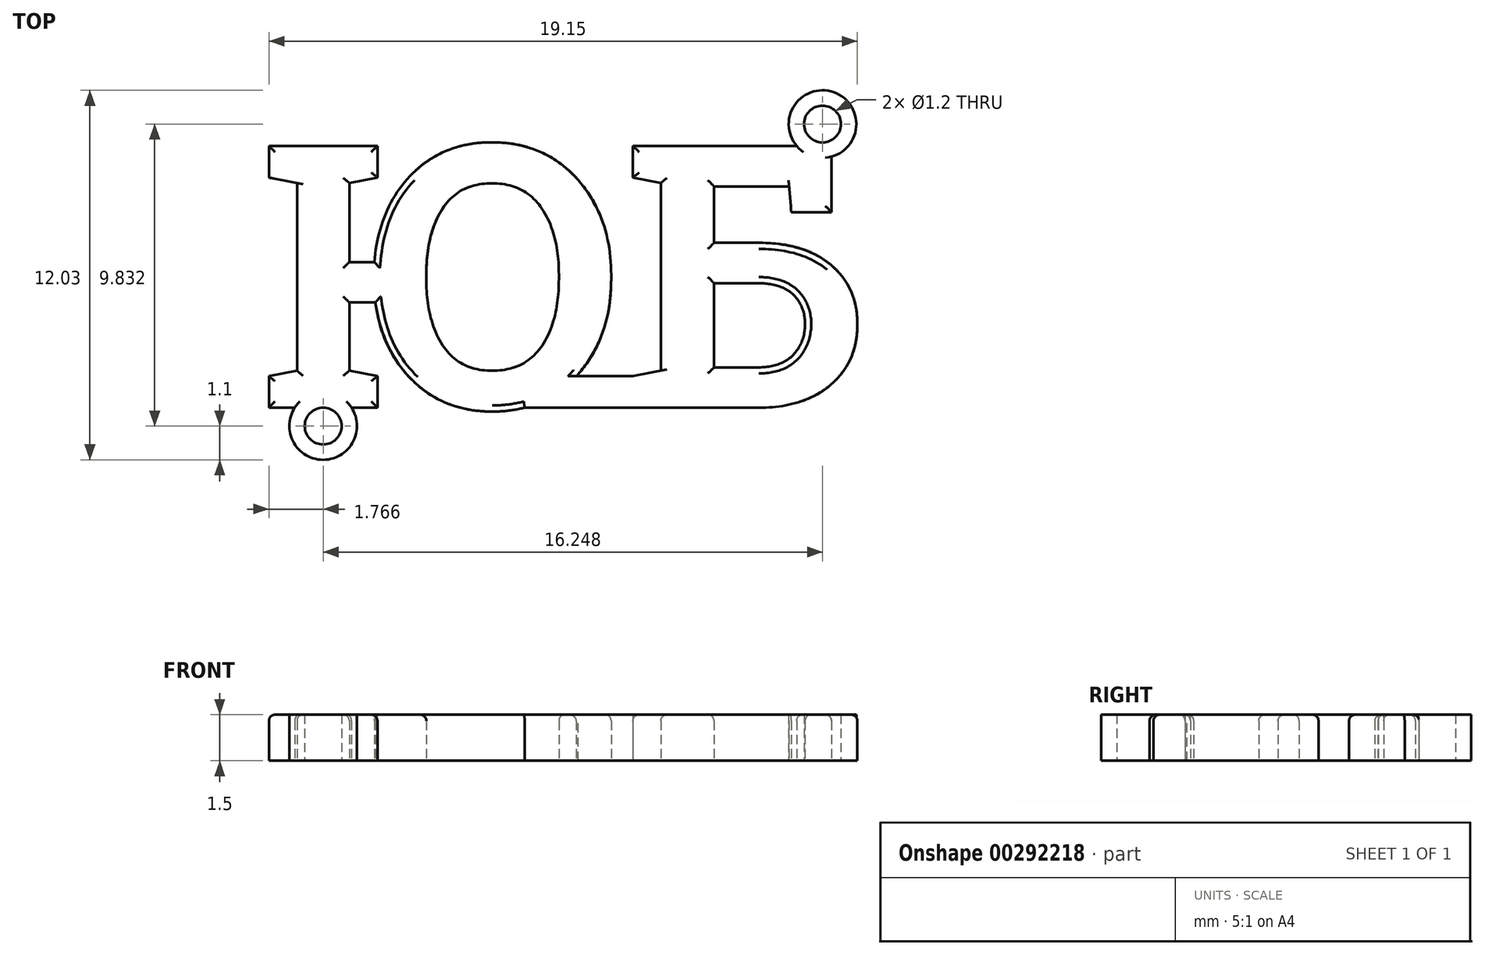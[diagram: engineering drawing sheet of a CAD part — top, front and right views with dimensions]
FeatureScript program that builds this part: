
annotation { "Feature Type Name" : "Feature", "Feature Type Description" : "" }
export const myFeature = defineFeature(function(context is Context, id is Id, definition is map)
    precondition{}
    {
        {
            var Q0;
            Q0=qCreatedBy(makeId("Top.planeOp"),FACE);
            var sketch = newSketch(context, id + "F0", { "sketchPlane" : qUnion([Q0])});
            skText(sketch, "E0", { "text": "ЮБ", "fontName": "RobotoSlab-Bold.ttf"});
            skCircle(sketch, "E1", {"center": v(-8.12, -0.6) * mm, "radius": 0.6 * mm});
            skCircle(sketch, "E2.0", {"center": v(-8.12, -0.6) * mm, "radius": 1.1 * mm});
            skPoint(sketch, "E3", {"position": v(-10, 0) * mm});
            skPoint(sketch, "E4", {"position": v(-8.12, 0) * mm});
            skPoint(sketch, "E5", {"position": v(-7.2, 0) * mm});
            skLineSegment(sketch, "E6", {"start": v(0, 0) * mm, "end": v(0, -7.24) * mm, "construction": true});
            skCircle(sketch, "E7.MirrorC", {"center": v(8.12, -0.6) * mm, "radius": 0.6 * mm, "construction": true});
            skCircle(sketch, "E8.MirrorC", {"center": v(8.12, -0.6) * mm, "radius": 1.1 * mm, "construction": true});
            skLineSegment(sketch, "E9", {"start": v(0, 4.32) * mm, "end": v(-11.86, 4.32) * mm, "construction": true});
            skPoint(sketch, "E9.endSnap0", {"position": v(-10, 4.32) * mm});
            skCircle(sketch, "E10.MirrorC", {"center": v(-8.12, 9.23) * mm, "radius": 0.6 * mm, "construction": true});
            skCircle(sketch, "E11.MirrorC", {"center": v(-8.12, 9.23) * mm, "radius": 1.1 * mm, "construction": true});
            skCircle(sketch, "E12.MirrorC", {"center": v(8.12, 9.23) * mm, "radius": 0.6 * mm});
            skLineSegment(sketch, "E13.bottom", {"start": v(1.96, 1.02) * mm, "end": v(-1.9, 1.02) * mm});
            skLineSegment(sketch, "E13.top", {"start": v(1.96, 0) * mm, "end": v(-1.9, 0) * mm});
            skLineSegment(sketch, "E13.left", {"start": v(1.96, 1.02) * mm, "end": v(1.96, 0) * mm});
            skLineSegment(sketch, "E13.right", {"start": v(-1.9, 1.02) * mm, "end": v(-1.9, 0) * mm});
            skCircle(sketch, "E14.MirrorC", {"center": v(8.12, 9.23) * mm, "radius": 1.1 * mm});
            skLineSegment(sketch, "E15", {"start": v(-9.89, 1.01) * mm, "end": v(-6.36, 1.01) * mm});
            skLineSegment(sketch, "E16", {"start": v(-8.12, 1.01) * mm, "end": v(-8.12, -0.92) * mm, "construction": true});
            const initialGuessF0  = {"E0": [-0.01, 0, 1, 0, 0.00863]};
            skSetInitialGuess(sketch, initialGuessF0);
            skSolve(sketch);
        }
        {
            var Q0;
            {var subQ9=sQuery(id+"F0.wireOp",EDGE,"cf95b76b-212f-4af7-b6d1-8cdce05abc63.top");Q0=makeQuery(id+"F0.imprint","IMPRINT",FACE,{"disambiguationData":[TD([[makeQuery(id+"F0.imprint","IMPRINT",EDGE,{"derivedFrom":subQ9}),1.0]])]});}
            var Q1;
            {var subQ1=sQuery(id+"F0.wireOp",EDGE,"E0.sketch_text.stroke-48");var subQ5=sQuery(id+"F0.wireOp",EDGE,"E0.sketch_text.stroke-47");var subQ6=makeQuery(id+"F0.imprint","INTERSECT",VERTEX,{"derivedFrom":[subQ5,subQ1]});Q1=makeQuery(id+"F0.imprint","IMPRINT",FACE,{"disambiguationData":[TD([[makeQuery(id+"F0.imprint","IMPRINT",EDGE,{"disambiguationData":[TD([[subQ6,1.0]])],"derivedFrom":subQ5}),1.0]])]});}
            var Q2;
            {var subQ1=sQuery(id+"F0.wireOp",EDGE,"E0.sketch_text.stroke-48");var subQ6=sQuery(id+"F0.wireOp",EDGE,"E0.sketch_text.stroke-47");var subQ7=makeQuery(id+"F0.imprint","INTERSECT",VERTEX,{"derivedFrom":[subQ6,subQ1]});Q2=makeQuery(id+"F0.imprint","IMPRINT",FACE,{"disambiguationData":[TD([[makeQuery(id+"F0.imprint","IMPRINT",EDGE,{"disambiguationData":[TD([[subQ7,1.0]])],"derivedFrom":subQ6}),-1.0]])]});}
            var Q3;
            {var subQ1=sQuery(id+"F0.wireOp",EDGE,"E0.sketch_text.stroke-19");var subQ6=sQuery(id+"F0.wireOp",EDGE,"E2.0");var subQ8=makeQuery(id+"F0.imprint","INTERSECT",VERTEX,{"derivedFrom":[subQ1,subQ6]});Q3=makeQuery(id+"F0.imprint","IMPRINT",FACE,{"disambiguationData":[TD([[makeQuery(id+"F0.imprint","IMPRINT",EDGE,{"disambiguationData":[TD([[subQ8,-1.0]])],"derivedFrom":subQ1}),-1.0]])]});}
            var Q4;
            {var subQ1=sQuery(id+"F0.wireOp",EDGE,"E0.sketch_text.stroke-19");var subQ3=sQuery(id+"F0.wireOp",EDGE,"E2.0");var subQ8=makeQuery(id+"F0.imprint","INTERSECT",VERTEX,{"derivedFrom":[subQ1,subQ3]});Q4=makeQuery(id+"F0.imprint","IMPRINT",FACE,{"disambiguationData":[TD([[makeQuery(id+"F0.imprint","IMPRINT",EDGE,{"disambiguationData":[TD([[subQ8,-1.0]])],"derivedFrom":subQ1}),1.0]])]});}
            var Q5;
            {var subQ1=sQuery(id+"F0.wireOp",EDGE,"E0.sketch_text.stroke-1");var subQ6=sQuery(id+"F0.wireOp",EDGE,"E0.sketch_text.stroke-0");var subQ7=makeQuery(id+"F0.imprint","INTERSECT",VERTEX,{"derivedFrom":[subQ6,subQ1]});Q5=makeQuery(id+"F0.imprint","IMPRINT",FACE,{"disambiguationData":[TD([[makeQuery(id+"F0.imprint","IMPRINT",EDGE,{"disambiguationData":[TD([[subQ7,1.0]])],"derivedFrom":subQ6}),1.0]])]});}
            var Q6;
            {var subQ0=sQuery(id+"F0.wireOp",EDGE,"E7.MirrorC");var subQ1=sQuery(id+"F0.wireOp",EDGE,"E0.sketch_text.stroke-48");var subQ2=makeQuery(id+"F0.imprint","INTERSECT",VERTEX,{"disambiguationData":[OD(0.0)],"derivedFrom":[subQ1,subQ0]});Q6=makeQuery(id+"F0.imprint","IMPRINT",FACE,{"disambiguationData":[TD([[makeQuery(id+"F0.imprint","IMPRINT",EDGE,{"disambiguationData":[TD([[subQ2,-1.0]])],"derivedFrom":subQ1}),-1.0]])]});}
            var Q7;
            {var subQ5=sQuery(id+"F0.wireOp",EDGE,"E13.right");Q7=makeQuery(id+"F0.imprint","IMPRINT",FACE,{"disambiguationData":[TD([[makeQuery(id+"F0.imprint","IMPRINT",EDGE,{"derivedFrom":subQ5}),1.0]])]});}
            var Q8;
            {var subQ0=sQuery(id+"F0.wireOp",EDGE,"E13.bottom");var subQ1=sQuery(id+"F0.wireOp",EDGE,"E0.sketch_text.stroke-12");var subQ2=makeQuery(id+"F0.imprint","INTERSECT",VERTEX,{"derivedFrom":[subQ1,subQ0]});Q8=makeQuery(id+"F0.imprint","IMPRINT",FACE,{"disambiguationData":[TD([[makeQuery(id+"F0.imprint","IMPRINT",EDGE,{"disambiguationData":[TD([[subQ2,-1.0]])],"derivedFrom":subQ1}),1.0]])]});}
            var Q9;
            {var subQ5=sQuery(id+"F0.wireOp",EDGE,"E13.left");Q9=makeQuery(id+"F0.imprint","IMPRINT",FACE,{"disambiguationData":[TD([[makeQuery(id+"F0.imprint","IMPRINT",EDGE,{"derivedFrom":subQ5}),-1.0]])]});}
            var Q10;
            {var subQ9=sQuery(id+"F0.wireOp",EDGE,"E0.sketch_text.stroke-34");Q10=makeQuery(id+"F0.imprint","IMPRINT",FACE,{"disambiguationData":[TD([[makeQuery(id+"F0.imprint","IMPRINT",EDGE,{"derivedFrom":subQ9}),-1.0]])]});}
            var Q11;
            {var subQ0=sQuery(id+"F0.wireOp",EDGE,"E14.MirrorC");var subQ1=sQuery(id+"F0.wireOp",EDGE,"E0.sketch_text.stroke-38");var subQ2=makeQuery(id+"F0.imprint","INTERSECT",VERTEX,{"derivedFrom":[subQ1,subQ0]});Q11=makeQuery(id+"F0.imprint","IMPRINT",FACE,{"disambiguationData":[TD([[makeQuery(id+"F0.imprint","IMPRINT",EDGE,{"disambiguationData":[TD([[subQ2,-1.0]])],"derivedFrom":subQ1}),1.0]])]});}
            var Q12;
            {var subQ0=sQuery(id+"F0.wireOp",EDGE,"E14.MirrorC");var subQ1=sQuery(id+"F0.wireOp",EDGE,"E0.sketch_text.stroke-38");var subQ2=makeQuery(id+"F0.imprint","INTERSECT",VERTEX,{"derivedFrom":[subQ1,subQ0]});Q12=makeQuery(id+"F0.imprint","IMPRINT",FACE,{"disambiguationData":[TD([[makeQuery(id+"F0.imprint","IMPRINT",EDGE,{"disambiguationData":[TD([[subQ2,-1.0]])],"derivedFrom":subQ1}),-1.0]])]});}
            var Q13;
            {var subQ1=sQuery(id+"F0.wireOp",EDGE,"E0.sketch_text.stroke-1");var subQ6=sQuery(id+"F0.wireOp",EDGE,"E0.sketch_text.stroke-0");var subQ7=makeQuery(id+"F0.imprint","INTERSECT",VERTEX,{"derivedFrom":[subQ6,subQ1]});Q13=makeQuery(id+"F0.imprint","IMPRINT",FACE,{"disambiguationData":[TD([[makeQuery(id+"F0.imprint","IMPRINT",EDGE,{"disambiguationData":[TD([[subQ7,1.0]])],"derivedFrom":subQ6}),-1.0]])]});}
            var Q14;
            {var subQ14=sQuery(id+"F0.wireOp",EDGE,"E0.sketch_text.stroke-2");Q14=makeQuery(id+"F0.imprint","IMPRINT",FACE,{"disambiguationData":[TD([[makeQuery(id+"F0.imprint","IMPRINT",EDGE,{"derivedFrom":subQ14}),-1.0]])]});}
            var Q15;
            {var subQ1=sQuery(id+"F0.wireOp",EDGE,"E0.sketch_text.stroke-19");var subQ6=sQuery(id+"F0.wireOp",EDGE,"E0.sketch_text.stroke-18");var subQ7=makeQuery(id+"F0.imprint","INTERSECT",VERTEX,{"derivedFrom":[subQ6,subQ1]});Q15=makeQuery(id+"F0.imprint","IMPRINT",FACE,{"disambiguationData":[TD([[makeQuery(id+"F0.imprint","IMPRINT",EDGE,{"disambiguationData":[TD([[subQ7,1.0]])],"derivedFrom":subQ6}),-1.0]])]});}
            extrude(context, id + "F1", {"entities" : qUnion([Q0, Q1, Q2, Q3, Q4, Q5, Q6, Q7, Q8, Q9, Q10, Q11, Q12, Q13, Q14, Q15]), "depth" : 1.5 * mm, "offsetDistance" : 25 * mm});
        }
        {
            var Q0;
            Q0=makeQuery(id+"F1.opExtrude","CAP_EDGE",EDGE,{"disambiguationData":[OSD([sQuery(id+"F0.wireOp",EDGE,"E0.sketch_text.stroke-39")])],"isStart":false});
            var Q1;
            Q1=makeQuery(id+"F1.opExtrude","CAP_EDGE",EDGE,{"disambiguationData":[OSD([sQuery(id+"F0.wireOp",EDGE,"E0.sketch_text.stroke-6")])],"isStart":false});
            var Q2;
            Q2=makeQuery(id+"F1.opExtrude","CAP_EDGE",EDGE,{"disambiguationData":[OSD([sQuery(id+"F0.wireOp",EDGE,"E0.sketch_text.stroke-1")])],"isStart":false});
            var Q3;
            Q3=makeQuery(id+"F1.opExtrude","CAP_EDGE",EDGE,{"disambiguationData":[OSD([sQuery(id+"F0.wireOp",EDGE,"E0.sketch_text.stroke-22")])],"isStart":false});
            var Q4;
            Q4=makeQuery(id+"F1.opExtrude","CAP_EDGE",EDGE,{"disambiguationData":[OSD([sQuery(id+"F0.wireOp",EDGE,"E0.sketch_text.stroke-0")])],"isStart":false});
            var Q5;
            Q5=makeQuery(id+"F1.opExtrude","CAP_EDGE",EDGE,{"disambiguationData":[OSD([sQuery(id+"F0.wireOp",EDGE,"E0.sketch_text.stroke-3")])],"isStart":false});
            var Q6;
            Q6=makeQuery(id+"F1.opExtrude","CAP_EDGE",EDGE,{"disambiguationData":[OSD([sQuery(id+"F0.wireOp",EDGE,"E0.sketch_text.stroke-2")])],"isStart":false});
            var Q7;
            Q7=makeQuery(id+"F1.opExtrude","CAP_EDGE",EDGE,{"disambiguationData":[OSD([sQuery(id+"F0.wireOp",EDGE,"E0.sketch_text.stroke-4")])],"isStart":false});
            var Q8;
            Q8=makeQuery(id+"F1.opExtrude","CAP_EDGE",EDGE,{"disambiguationData":[OSD([sQuery(id+"F0.wireOp",EDGE,"E0.sketch_text.stroke-5")])],"isStart":false});
            var Q9;
            Q9=makeQuery(id+"F1.opExtrude","CAP_EDGE",EDGE,{"disambiguationData":[OSD([sQuery(id+"F0.wireOp",EDGE,"E0.sketch_text.stroke-15")])],"isStart":false});
            var Q10;
            Q10=makeQuery(id+"F1.opExtrude","CAP_EDGE",EDGE,{"disambiguationData":[OSD([sQuery(id+"F0.wireOp",EDGE,"E0.sketch_text.stroke-16")])],"isStart":false});
            var Q11;
            Q11=makeQuery(id+"F1.opExtrude","CAP_EDGE",EDGE,{"disambiguationData":[OSD([sQuery(id+"F0.wireOp",EDGE,"E0.sketch_text.stroke-14")])],"isStart":false});
            var Q12;
            Q12=makeQuery(id+"F1.opExtrude","CAP_EDGE",EDGE,{"disambiguationData":[OSD([sQuery(id+"F0.wireOp",EDGE,"E0.sketch_text.stroke-13")])],"isStart":false});
            var Q13;
            Q13=makeQuery(id+"F1.opExtrude","CAP_EDGE",EDGE,{"disambiguationData":[OSD([sQuery(id+"F0.wireOp",EDGE,"E0.sketch_text.stroke-49"),sQuery(id+"F0.wireOp",EDGE,"E13.top")])],"isStart":false});
            var Q14;
            Q14=makeQuery(id+"F1.opExtrude","CAP_EDGE",EDGE,{"disambiguationData":[OSD([sQuery(id+"F0.wireOp",EDGE,"E0.sketch_text.stroke-57")])],"isStart":false});
            var Q15;
            Q15=makeQuery(id+"F1.opExtrude","CAP_EDGE",EDGE,{"disambiguationData":[OSD([sQuery(id+"F0.wireOp",EDGE,"E0.sketch_text.stroke-51")])],"isStart":false});
            var Q16;
            Q16=makeQuery(id+"F1.opExtrude","CAP_EDGE",EDGE,{"disambiguationData":[OSD([sQuery(id+"F0.wireOp",EDGE,"E0.sketch_text.stroke-43")])],"isStart":false});
            var Q17;
            Q17=makeQuery(id+"F1.opExtrude","CAP_EDGE",EDGE,{"disambiguationData":[OSD([sQuery(id+"F0.wireOp",EDGE,"E0.sketch_text.stroke-42")])],"isStart":false});
            var Q18;
            Q18=makeQuery(id+"F1.opExtrude","CAP_EDGE",EDGE,{"disambiguationData":[OSD([sQuery(id+"F0.wireOp",EDGE,"E0.sketch_text.stroke-40")])],"isStart":false});
            var Q19;
            Q19=makeQuery(id+"F1.opExtrude","CAP_EDGE",EDGE,{"disambiguationData":[OSD([sQuery(id+"F0.wireOp",EDGE,"E0.sketch_text.stroke-36")])],"isStart":false});
            var Q20;
            Q20=makeQuery(id+"F1.opExtrude","CAP_EDGE",EDGE,{"disambiguationData":[OSD([sQuery(id+"F0.wireOp",EDGE,"E0.sketch_text.stroke-35")])],"isStart":false});
            var Q21;
            Q21=makeQuery(id+"F1.opExtrude","CAP_EDGE",EDGE,{"disambiguationData":[OSD([sQuery(id+"F0.wireOp",EDGE,"E0.sketch_text.stroke-37")])],"isStart":false});
            var Q22;
            Q22=makeQuery(id+"F1.opExtrude","CAP_EDGE",EDGE,{"disambiguationData":[OSD([sQuery(id+"F0.wireOp",EDGE,"E0.sketch_text.stroke-38")])],"isStart":false});
            var Q23;
            Q23=makeQuery(id+"F1.opExtrude","CAP_EDGE",EDGE,{"disambiguationData":[OSD([sQuery(id+"F0.wireOp",EDGE,"E0.sketch_text.stroke-21")])],"isStart":false});
            var Q24;
            Q24=makeQuery(id+"F1.opExtrude","CAP_EDGE",EDGE,{"disambiguationData":[OSD([sQuery(id+"F0.wireOp",EDGE,"E0.sketch_text.stroke-20")])],"isStart":false});
            var Q25;
            {var subQ0=sQuery(id+"F0.wireOp",EDGE,"E0.sketch_text.stroke-19");Q25=makeQuery(id+"F1.opExtrude","CAP_EDGE",EDGE,{"disambiguationData":[OSD([subQ0]),TDD([makeQuery(id+"F0.imprint","IMPRINT",EDGE,{"disambiguationData":[TD([[makeQuery(id+"F0.imprint","INTERSECT",VERTEX,{"derivedFrom":[subQ0,sQuery(id+"F0.wireOp",EDGE,"E0.sketch_text.stroke-20")]}),1.0]])],"derivedFrom":subQ0})])],"isStart":false});}
            var Q26;
            {var subQ0=sQuery(id+"F0.wireOp",EDGE,"E0.sketch_text.stroke-19");Q26=makeQuery(id+"F1.opExtrude","CAP_EDGE",EDGE,{"disambiguationData":[OSD([subQ0]),TDD([makeQuery(id+"F0.imprint","IMPRINT",EDGE,{"disambiguationData":[TD([[makeQuery(id+"F0.imprint","INTERSECT",VERTEX,{"derivedFrom":[sQuery(id+"F0.wireOp",EDGE,"E0.sketch_text.stroke-18"),subQ0]}),-1.0]])],"derivedFrom":subQ0})])],"isStart":false});}
            var Q27;
            Q27=makeQuery(id+"F1.opExtrude","CAP_EDGE",EDGE,{"disambiguationData":[OSD([sQuery(id+"F0.wireOp",EDGE,"E0.sketch_text.stroke-18")])],"isStart":false});
            var Q28;
            Q28=makeQuery(id+"F1.opExtrude","CAP_EDGE",EDGE,{"disambiguationData":[OSD([sQuery(id+"F0.wireOp",EDGE,"E0.sketch_text.stroke-17")])],"isStart":false});
            var Q29;
            Q29=makeQuery(id+"F1.opExtrude","CAP_EDGE",EDGE,{"disambiguationData":[OSD([sQuery(id+"F0.wireOp",EDGE,"E0.sketch_text.stroke-32")])],"isStart":false});
            fillet(context, id + "F2", {"entities" : qUnion([Q0, Q1, Q2, Q3, Q4, Q5, Q6, Q7, Q8, Q9, Q10, Q11, Q12, Q13, Q14, Q15, Q16, Q17, Q18, Q19, Q20, Q21, Q22, Q23, Q24, Q25, Q26, Q27, Q28, Q29]), "radius" : 0.2 * mm, "tangentPropagation" : true, "allowEdgeOverflow" : false});
        }
    });
